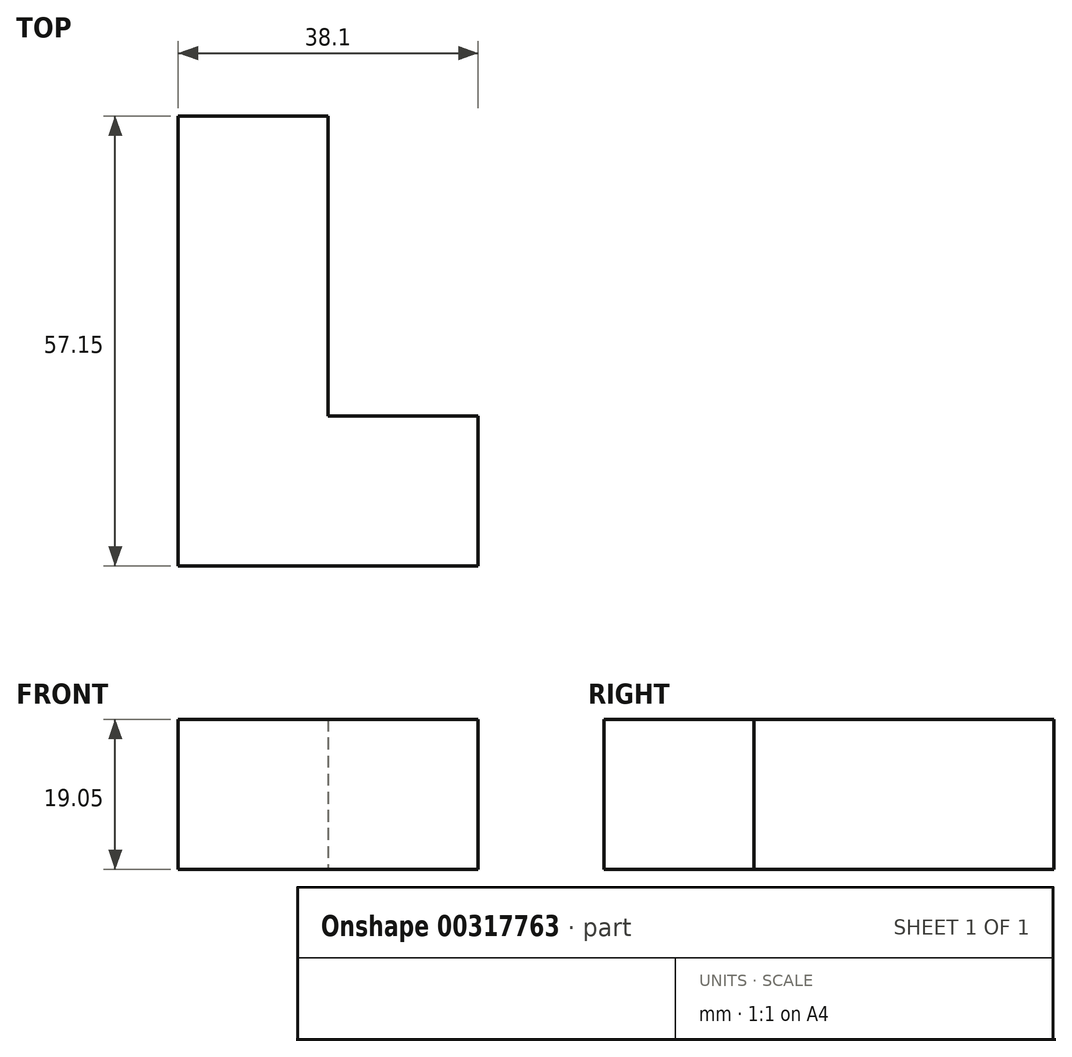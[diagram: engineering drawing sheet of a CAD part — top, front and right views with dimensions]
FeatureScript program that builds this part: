
annotation { "Feature Type Name" : "Feature", "Feature Type Description" : "" }
export const myFeature = defineFeature(function(context is Context, id is Id, definition is map)
    precondition{}
    {
        {
            var Q0;
            Q0=qCreatedBy(makeId("Top.planeOp"),FACE);
            var sketch = newSketch(context, id + "F0", { "sketchPlane" : qUnion([Q0])});
            skLineSegment(sketch, "E0.bottom", {"start": v(0, 0) * mm, "end": v(-19.05, 0) * mm});
            skLineSegment(sketch, "E0.top", {"start": v(0, 57.15) * mm, "end": v(-19.05, 57.15) * mm});
            skLineSegment(sketch, "E0.left", {"start": v(0, 19.05) * mm, "end": v(0, 57.15) * mm});
            skLineSegment(sketch, "E0.right", {"start": v(-19.05, 0) * mm, "end": v(-19.05, 57.15) * mm});
            skLineSegment(sketch, "E1.bottom", {"start": v(0, 0) * mm, "end": v(19.05, 0) * mm});
            skLineSegment(sketch, "E1.top", {"start": v(0, 19.05) * mm, "end": v(19.05, 19.05) * mm});
            skLineSegment(sketch, "E1.right", {"start": v(19.05, 0) * mm, "end": v(19.05, 19.05) * mm});
            skSolve(sketch);
        }
        {
            var Q0;
            Q0 = qSketchRegion(id + "F0", true);
            extrude(context, id + "F1", {"entities" : qUnion([Q0]), "depth" : 19.05 * mm});
        }
    });
